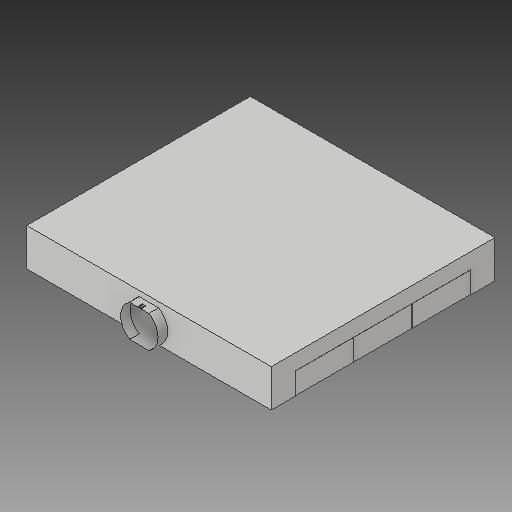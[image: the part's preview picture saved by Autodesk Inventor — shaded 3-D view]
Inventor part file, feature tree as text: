
AUTODESK INVENTOR PART (.ipt)
format: ipt  version: 2017 (Build 210142000, 142)  size: 323,584 bytes
history: native  units: in
note: dims shown in document units (in); Inventor stores cm internally (conversion verified against a paired STEP export)
features: extrude x6, sketch x5, delete_face x1
ambient origin geometry x8: Origin, YZ Plane, XZ Plane, XY Plane, X Axis, Y Axis, Z Axis, Center Point
bodies: Solid1 (feature_tree)
feature tree (12):
  extrude  "cubicals"  Depth=12.0in
  extrude  "floor"  Depth=2.5in
  extrude  "walls"  Depth=0.0833in
  sketch  "Sketch4"  dims[d10=0.0833in d95=0.0833in]
  extrude  "connection"  Depth=0.0833in
  extrude  "connection cut"  Depth=2.5in
  extrude  "ceiling"  Depth=2.5in
  delete_face  "Delete Face1"
  sketch  "Sketch2"  dims[d2=4.5in d3=0.0in d4=12.0in]
  sketch  "Sketch3"  dims[d5=8.0in d7=2.5in]
  sketch  "Sketch6"  dims[d97=0.0833in d98=0.0833in]
  sketch  "Sketch7"  dims[d99=12.0in d100=8.0in d102=0.0833in d103=0.0833in d104=0.0833in d105=0.0833in d106=12.0in d107=8.0in d109=0.0833in d110=0.0833in d111=0.0833in d112=0.0833in d113=2.5in d114=2.5in d115=3.0in d117=3.0in d118=6.0in d120=6.0in d121=1.0in d122=0.0in d128=1.0in d129=1.0in d130=1.0in d131=1.0in d132=1.0in d133=1.0in d134=7.7746in d135=0.0in d160=1.0in d161=0.0in d171=1.0in d172=0.0in d173=1.0in d174=0.0in d175=4.0in d176=0.5833in d177=3.8873in d178=3.8873in d179=1.7083in d180=0.0625in d181=0.0625in d182=1.6458in d183=0.25in d184=0.125in d185=0.0884in d186=45.0deg d187=3.3333in d188=1.0in d189=1.0in d190=0.125in]
